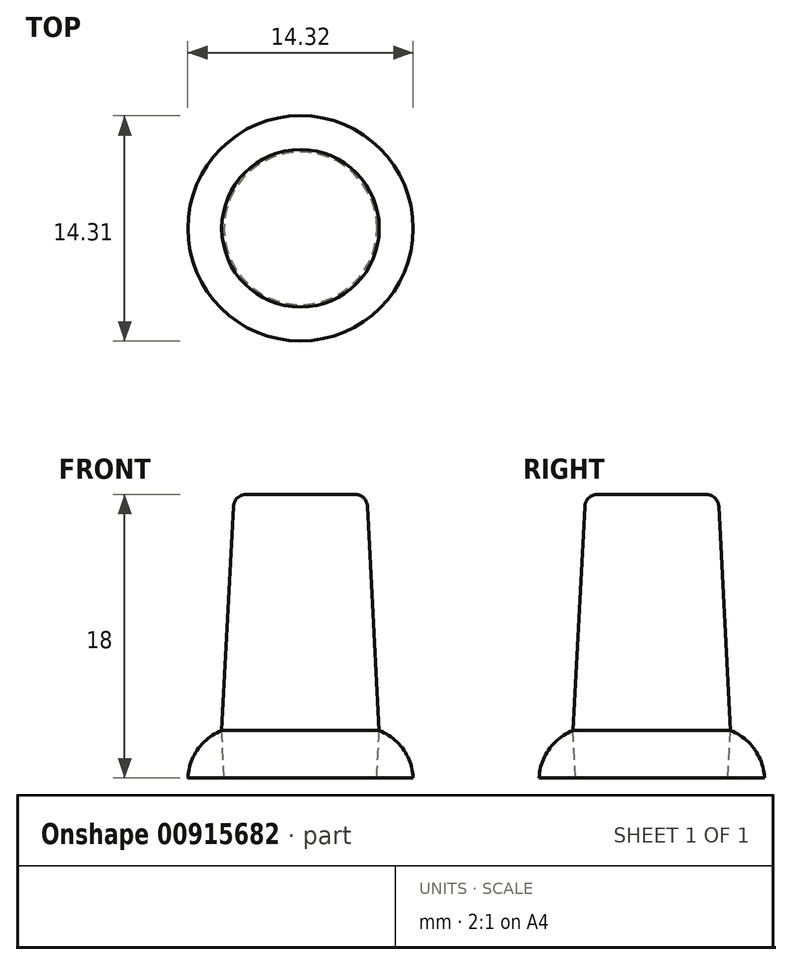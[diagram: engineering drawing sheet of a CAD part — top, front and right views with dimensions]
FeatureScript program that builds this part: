
annotation { "Feature Type Name" : "Feature", "Feature Type Description" : "" }
export const myFeature = defineFeature(function(context is Context, id is Id, definition is map)
    precondition{}
    {
        {
            var Q0;
            Q0=qCreatedBy(makeId("Top.planeOp"),FACE);
            var sketch = newSketch(context, id + "F0", { "sketchPlane" : qUnion([Q0])});
            skCircle(sketch, "E0", {"center": v(-26.88, 32.42) * mm, "radius": 9 * mm});
            skCircle(sketch, "E1", {"center": v(-26.88, 32.42) * mm, "radius": 5 * mm});
            skCircle(sketch, "E2", {"center": v(-26.88, 32.42) * mm, "radius": 7 * mm});
            skSolve(sketch);
        }
        {
            var Q0;
            Q0=makeQuery(id+"F0.imprint","IMPRINT",FACE,{"disambiguationData":[TD([[makeQuery(id+"F0.imprint","IMPRINT",EDGE,{"derivedFrom":sQuery(id+"F0.wireOp",EDGE,"E1")}),1.0]])]});
            extrude(context, id + "F1", {"entities" : qUnion([Q0]), "depth" : 15 * mm, "offsetDistance" : 25 * mm, "hasDraft" : true, "draftAngle" : 3 * degree, "draftPullDirection" : true});
        }
        {
            var Q0;
            Q0=makeQuery(id+"F0.imprint","IMPRINT",FACE,{"disambiguationData":[TD([[makeQuery(id+"F0.imprint","IMPRINT",EDGE,{"derivedFrom":sQuery(id+"F0.wireOp",EDGE,"E1")}),-1.0]])]});
            extrude(context, id + "F2", {"entities" : qUnion([Q0]), "depth" : 4 * mm, "offsetDistance" : 25 * mm, "hasDraft" : true, "draftAngle" : 3 * degree, "draftPullDirection" : true});
        }
        {
            var Q0;
            Q0=makeQuery(id+"F1.opExtrude","CAP_EDGE",EDGE,{"disambiguationData":[OSD([sQuery(id+"F0.wireOp",EDGE,"E1")])],"isStart":false});
            fillet(context, id + "F3", {"entities" : qUnion([Q0]), "radius" : 0.8 * mm, "allowEdgeOverflow" : false});
        }
        {
            var Q0;
            Q0=makeQuery(id+"F2.opExtrude","SWEPT_BODY",BODY,{"disambiguationData":[OSD([sQuery(id+"F0.wireOp",EDGE,"E1"),sQuery(id+"F0.wireOp",EDGE,"E2")])]});
            deleteBodies(context, id + "F4", {"entities" : qUnion([Q0])});
        }
        {
            var Q0;
            Q0=makeQuery(id+"F0.imprint","IMPRINT",FACE,{"disambiguationData":[TD([[makeQuery(id+"F0.imprint","IMPRINT",EDGE,{"derivedFrom":sQuery(id+"F0.wireOp",EDGE,"E1")}),-1.0]])]});
            extrude(context, id + "F5", {"entities" : qUnion([Q0]), "oppositeDirection" : true, "depth" : 3 * mm, "offsetDistance" : 25 * mm, "hasDraft" : true, "draftAngle" : 3 * degree});
        }
        {
            var Q0;
            Q0=makeQuery(id+"F5.opExtrude","CAP_EDGE",EDGE,{"disambiguationData":[OSD([sQuery(id+"F0.wireOp",EDGE,"E2")])],"isStart":true});
            fillet(context, id + "F6", {"entities" : qUnion([Q0]), "radius" : 3.4 * mm, "tangentPropagation" : true, "allowEdgeOverflow" : false});
        }
    });
